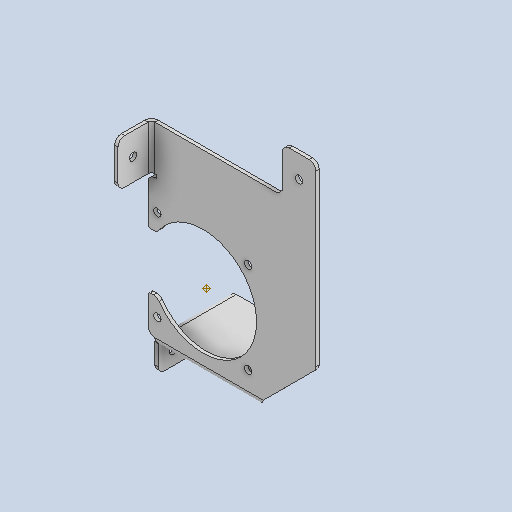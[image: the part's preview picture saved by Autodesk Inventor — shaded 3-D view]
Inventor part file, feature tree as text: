
AUTODESK INVENTOR PART (.ipt)
format: ipt  version: 2022.1 (Build 261234000, 234)  size: 322,560 bytes
history: native  units: mm
features: other x14, sheet_metal_op x8, reference x7, sketch x6, chamfer x3, hole x2
ambient origin geometry x8: Origin, YZ Plane, XZ Plane, XY Plane, X Axis, Y Axis, Z Axis, Center Point
bodies: Solid1 (feature_tree)
feature tree (40):
  sheet_metal_op  "Face1"
  sheet_metal_op  "Face2"
  sheet_metal_op  "Face3"
  sheet_metal_op  "Flange1"
  hole  "Hole1"  [1 undecoded]
  hole  "Hole2"  [1 undecoded]
  chamfer  "Corner Round1"
  chamfer  "Corner Round2"
  chamfer  "Corner Round3"
  other  "Corner Chamfer1"
  sketch  "Sketch1"  dims[d6=3.0mm d9=45.0deg]
  reference  "Reference3"
  reference  "Reference4"
  other  "Plate1"
  reference  "Reference5"
  reference  "Reference6"
  reference  "Reference7"
  reference  "Reference8"
  reference  "Reference9"
  sketch  "Sketch3"  dims[d10=210.0mm d11=30.0mm]
  other  "Plate2"
  sheet_metal_op  "Bend1"
  sketch  "Sketch4"  dims[d13=96.0mm]
  other  "Plate3"
  sheet_metal_op  "Bend2"
  sketch  "Sketch5"  dims[d18=40.0mm]
  other  "Plate4"
  sheet_metal_op  "Bend3"
  sheet_metal_op  "Corner1"
  sketch  "Sketch6"  dims[d19=40.0mm]
  sketch  "Sketch7"  dims[d20=30.0mm d21=3.0mm d22=3.0mm d23=1.5mm d24=6.0mm d25=3.0mm d26=45.0deg d27=70.0mm d28=3.0mm d29=3.0mm d30=1.5mm d31=6.0mm d32=3.0mm d33=3.0mm d34=1.5mm d35=6.0mm d36=3.0mm d37=30.0mm d38=90.0deg d39=3.0mm d40=12.0mm d41=3.0mm d42=3.0mm d43=50.0mm d44=6.6mm d45=6.0mm d46=12.6mm d47=2.0mm d48=90.0deg d49=3.0mm d50=20.594885mm d51=50.0mm d52=40.0mm d53=6.6mm d54=6.0mm d55=4.0mm d56=2.0mm d57=90.0deg d58=8.0mm d59=20.594885mm d60=6.0mm d61=6.0mm d62=2.0mm d63=4.0mm d64=6.0mm d65=45.0deg d66=120.0mm d67=100.0mm]
  other  "<userpath>\Desktop\PDM\ProyectoRobotPallet\RobotPallet.iam"
  other  "RobotPallet.iam"
  other  "EstructuraInferior - Soldadura:1"
  other  "Frame_Base:1"
  other  "ISO 10799-2 40x40x2 - 437.5:2"
  other  "ISO 10799-2 40x40x2 - 2899.41:1"
  other  "Sistema de movimiento:2"
  other  "bg-95x80-885950205312:1"
  other  "Definición1"
note: 2 required parameter values undecoded (feature->parameter linkage not recoverable at this tier; creation-order binding heuristic only, values carry confidence <= 0.55)
